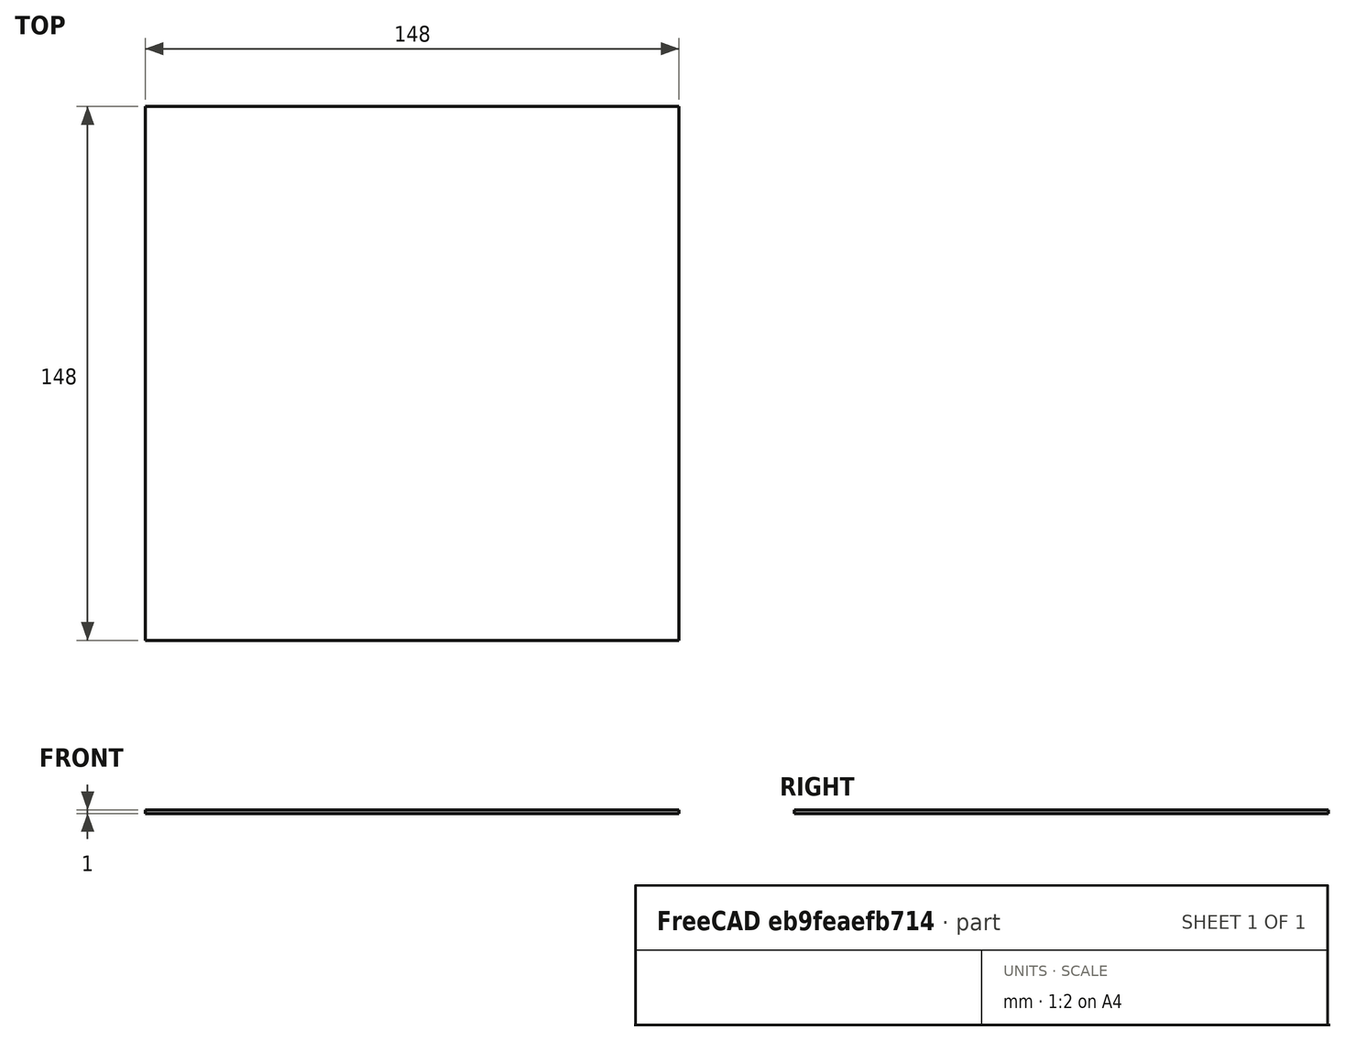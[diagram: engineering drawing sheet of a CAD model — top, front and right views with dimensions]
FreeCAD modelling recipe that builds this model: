
FCSTD DOCUMENT  (FreeCAD 0.21R32532 (Git))
Label: rotator
License: All rights reserved
LicenseURL: http://en.wikipedia.org/wiki/All_rights_reserved
objects: Sketcher::SketchObject×3, PartDesign::SubShapeBinder×2, PartDesign::Pad×1, Part::FeaturePython×1, PartDesign::Body×1
note: 8 computed .brp shape members not serialized (recipe doc carries the construction recipe); baked Part::Feature solids carry a one-line shape summary decoded from their .brp

FEATURE [Sketcher::SketchObject] Sketch
  FullyConstrained = true
  MapMode = 5
  Support = -> [XY_Plane]
  expr: Constraints[20] = (51.15 + 63.9) / 2
  sketch-geometry (9):
    g0: Circle CenterX=-7.1e-15 CenterY=33.2121 CenterZ=0 NormalX=0 NormalY=0 NormalZ=1 AngleXU=0 Radius=2.5
    g1: Circle CenterX=28.7625 CenterY=-16.606 CenterZ=0 NormalX=0 NormalY=0 NormalZ=1 AngleXU=0 Radius=2.5
    g2: Circle CenterX=-28.7625 CenterY=-16.606 CenterZ=0 NormalX=0 NormalY=0 NormalZ=1 AngleXU=0 Radius=2.5
    g3: LineSegment StartX=-28.7625 StartY=-16.606 StartZ=0 EndX=28.7625 EndY=-16.606 EndZ=0
    g4: LineSegment StartX=28.7625 StartY=-16.606 StartZ=0 EndX=-7.1e-15 EndY=33.2121 EndZ=0
    g5: LineSegment StartX=-7.1e-15 StartY=33.2121 StartZ=0 EndX=-28.7625 EndY=-16.606 EndZ=0
    g6: LineSegment StartX=-7.1e-15 StartY=33.2121 StartZ=0 EndX=0 EndY=0 EndZ=0
    g7: LineSegment StartX=0 StartY=0 StartZ=0 EndX=-28.7625 EndY=-16.606 EndZ=0
    g8: LineSegment StartX=0 StartY=0 StartZ=0 EndX=28.7625 EndY=-16.606 EndZ=0
  constraints (21):
    c: PointOnObject(g0,g-2)
    c: Coincident(g3,g2)
    c: Coincident(g3,g1)
    c: Coincident(g3,g4)
    c: Coincident(g4,g0)
    c: Coincident(g4,g5)
    c: Coincident(g5,g3)
    c: Coincident(g6,g0)
    c: Coincident(g6,g-1)
    c: Coincident(g6,g7)
    c: Coincident(g7,g2)
    c: Coincident(g6,g8)
    c: Coincident(g8,g1)
    c: Equal(g8,g7)
    c: Equal(g7,g6)
    c: Equal(g3,g4)
    c: Equal(g4,g5)
    c: Equal(g0,g2)
    c: Equal(g2,g1)
    c: Diameter(g0) = 5
    c: DistanceX(g3,g3) = 57.525
FEATURE [Sketcher::SketchObject] Sketch001
  FullyConstrained = true
  MapMode = 5
  Support = -> [XY_Plane]
  sketch-geometry (5):
    g0: LineSegment StartX=-74 StartY=-74 StartZ=0 EndX=-74 EndY=74 EndZ=0
    g1: LineSegment StartX=-74 StartY=74 StartZ=0 EndX=74 EndY=74 EndZ=0
    g2: LineSegment StartX=74 StartY=74 StartZ=0 EndX=74 EndY=-74 EndZ=0
    g3: LineSegment StartX=74 StartY=-74 StartZ=0 EndX=-74 EndY=-74 EndZ=0
    g4: GeomPoint X=0 Y=0 Z=0
  constraints (12):
    c: Coincident(g0,g1)
    c: Coincident(g1,g2)
    c: Coincident(g2,g3)
    c: Coincident(g3,g0)
    c: Horizontal(g1)
    c: Horizontal(g3)
    c: Vertical(g0)
    c: Vertical(g2)
    c: Symmetric(g1,g0,g4)
    c: Coincident(g4,g-1)
    c: Equal(g1,g2)
    c: DistanceX(g1,g1) = 148
FEATURE [PartDesign::Pad] Pad
  Direction = (0,0,1)
  Length = 1
  Length2 = 10
  Profile = -> Sketch001
  ReferenceAxis = -> Sketch001 [N_Axis]
  Type = 0
FEATURE [Sketcher::SketchObject] Sketch002
  AttachmentOffset = pos=(0,0,0) rot=(0,0,1;0.785398rad)
  FullyConstrained = true
  MapMode = 5
  Placement = pos=(0,0,0) rot=(0,0,1;0.785398rad)
  Support = -> [XY_Plane]
  expr: Constraints[7] = 93.55 mm
  sketch-geometry (6):
    g0: ArcOfCircle CenterX=81.75 CenterY=0 CenterZ=0 NormalX=0 NormalY=0 NormalZ=1 AngleXU=0 Radius=3.1 StartAngle=1.5708 EndAngle=4.71239
    g1: ArcOfCircle CenterX=90.45 CenterY=0 CenterZ=0 NormalX=0 NormalY=0 NormalZ=1 AngleXU=0 Radius=3.1 StartAngle=4.71239 EndAngle=7.85398
    g2: LineSegment StartX=81.75 StartY=-3.1 StartZ=0 EndX=90.45 EndY=-3.1 EndZ=0
    g3: LineSegment StartX=90.45 StartY=3.1 StartZ=0 EndX=81.75 EndY=3.1 EndZ=0
    g4: GeomPoint X=78.65 Y=0 Z=0
    g5: GeomPoint X=93.55 Y=0 Z=0
  constraints (14):
    c: Tangent(g0,g2) = -1.5708
    c: Tangent(g2,g1) = -1.5708
    c: Tangent(g1,g3) = -1.5708
    c: Tangent(g3,g0) = -1.5708
    c: Equal(g0,g1)
    c: PointOnObject(g0,g-1)
    c: PointOnObject(g1,g-1)
    c: DistanceX(g5) = 93.55
    c: DistanceX(g4) = 78.65
    c: DistanceY(g0,g0) = 6.2
    c: PointOnObject(g4,g-1)
    c: PointOnObject(g4,g0)
    c: PointOnObject(g5,g-1)
    c: PointOnObject(g5,g1)
FEATURE [Part::FeaturePython] Array  # Draft array (typed FeaturePython)
  AlwaysSyncPlacement = false
  Angle = 360
  ArrayType = 1
  Axis = (0,0,1)
  Base = -> Sketch002
  Center = (0,0,0)
  Count = 4
  ExpandArray = false
  Fuse = false
  IntervalAxis = (0,0,0)
  IntervalX = (50,0,0)
  IntervalY = (0,50,0)
  IntervalZ = (0,0,50)
  NumberCircles = 3
  NumberPolar = 4
  NumberX = 2
  NumberY = 2
  NumberZ = 1
  PlacementList = 4 placements: [(0,0,0),(0,0,0),(0,0,0),(0,0,0)]
  RadialDistance = 50
  ScaleList = (4) [(1,1,1),(1,1,1),(1,1,1),(1,1,1)]
  Symmetry = 1
  TangentialDistance = 25
FEATURE [PartDesign::SubShapeBinder] Binder
  BindCopyOnChange = 0
  BindMode = 0
  ClaimChildren = true
  Context = -> Body [Binder.]
  Fuse = false
  MakeFace = true
  OffsetFill = false
  OffsetIntersection = false
  OffsetJoinType = 0
  OffsetOpenResult = false
  PartialLoad = false
  Relative = true
  Support = -> [Array]
  _Version = 2
FEATURE [PartDesign::SubShapeBinder] Binder001
  BindCopyOnChange = 0
  BindMode = 0
  ClaimChildren = true
  Context = -> Body [Binder001.]
  Fuse = false
  MakeFace = true
  OffsetFill = false
  OffsetIntersection = false
  OffsetJoinType = 0
  OffsetOpenResult = false
  PartialLoad = false
  Relative = true
  Support = -> [Sketch]
  _Version = 2
FEATURE [PartDesign::Body] Body
  Group = -> [Sketch,Sketch001,Pad,Sketch002,Binder,Binder001]
  Origin = -> Origin
  Tip = -> Pad
